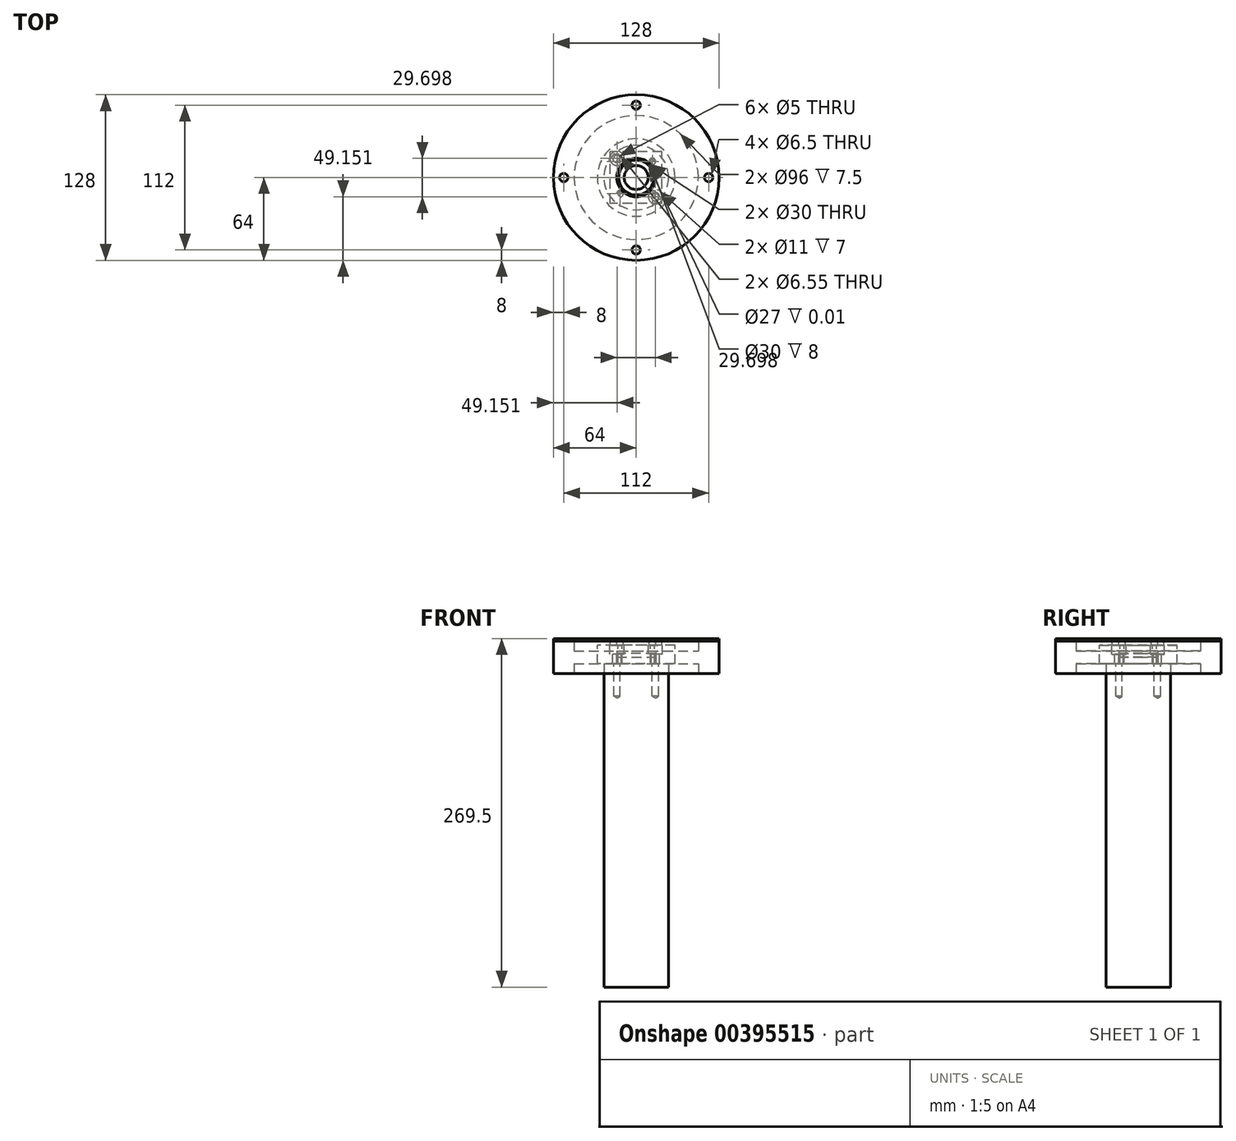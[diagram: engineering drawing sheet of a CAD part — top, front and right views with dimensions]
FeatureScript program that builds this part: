
annotation { "Feature Type Name" : "Feature", "Feature Type Description" : "" }
export const myFeature = defineFeature(function(context is Context, id is Id, definition is map)
    precondition{}
    {
        {
            var Q0;
            Q0=qCreatedBy(makeId("Front.planeOp"),FACE);
            var sketch = newSketch(context, id + "F0", { "sketchPlane" : qUnion([Q0])});
            skLineSegment(sketch, "E0.bottom", {"start": v(-64, 0) * mm, "end": v(-48, 0) * mm});
            skLineSegment(sketch, "E0.top", {"start": v(-64, -25) * mm, "end": v(-48, -25) * mm});
            skLineSegment(sketch, "E0.left", {"start": v(-64, 0) * mm, "end": v(-64, -25) * mm});
            skLineSegment(sketch, "E0.right", {"start": v(-15, -7.5) * mm, "end": v(-15, -17.5) * mm});
            skLineSegment(sketch, "E1", {"start": v(-48, 0) * mm, "end": v(-48, -7.5) * mm});
            skPoint(sketch, "E2.oppositeSnap0", {"position": v(-15, -17.5) * mm});
            skLineSegment(sketch, "E2.bottom", {"start": v(-15, -7.5) * mm, "end": v(-48, -7.5) * mm});
            skLineSegment(sketch, "E2.top", {"start": v(-15, -17.5) * mm, "end": v(-48, -17.5) * mm});
            skLineSegment(sketch, "E3.trimOffspring", {"start": v(-48, -17.5) * mm, "end": v(-48, -25) * mm});
            skSolve(sketch);
        }
        {
            var Q0;
            Q0=qCreatedBy(makeId("Front.planeOp"),FACE);
            var sketch = newSketch(context, id + "F1", { "sketchPlane" : qUnion([Q0])});
            skLineSegment(sketch, "E4.bottom", {"start": v(-25, -267.5) * mm, "end": v(0, -267.5) * mm});
            skLineSegment(sketch, "E4.top", {"start": v(-25, -17.5) * mm, "end": v(-15, -17.5) * mm});
            skLineSegment(sketch, "E4.left", {"start": v(-25, -267.5) * mm, "end": v(-25, -17.5) * mm});
            skLineSegment(sketch, "E4.right", {"start": v(0, -267.5) * mm, "end": v(0, -12.5) * mm});
            skLineSegment(sketch, "E5.top", {"start": v(0, -12.5) * mm, "end": v(-15, -12.5) * mm});
            skLineSegment(sketch, "E5.right", {"start": v(-15, -17.5) * mm, "end": v(-15, -12.5) * mm});
            skSolve(sketch);
        }
        {
            var Q0;
            Q0=makeQuery(id+"F1.imprint","IMPRINT",FACE,{"disambiguationData":[TD([[makeQuery(id+"F1.imprint","IMPRINT",EDGE,{"derivedFrom":sQuery(id+"F1.wireOp",EDGE,"E4.bottom")}),1.0]])]});
            var Q1;
            Q1=sQuery(id+"F1.wireOp",EDGE,"E4.right");
            revolve(context, id + "F2", {"entities" : qUnion([Q0]), "axis" : qUnion([Q1]), "revolveType" : RevolveType.FULL});
        }
        {
            var Q0;
            Q0=makeQuery(id+"F0.imprint","IMPRINT",FACE,{"disambiguationData":[TD([[makeQuery(id+"F0.imprint","IMPRINT",EDGE,{"derivedFrom":sQuery(id+"F0.wireOp",EDGE,"E0.bottom")}),-1.0]])]});
            var Q1;
            Q1=sQuery(id+"F1.wireOp",EDGE,"E4.right");
            revolve(context, id + "F3", {"entities" : qUnion([Q0]), "axis" : qUnion([Q1]), "revolveType" : RevolveType.FULL});
        }
        {
            var Q0;
            Q0=qCreatedBy(makeId("Top.planeOp"),FACE);
            var sketch = newSketch(context, id + "F4", { "sketchPlane" : qUnion([Q0])});
            skCircle(sketch, "E6", {"center": v(0, 0) * mm, "radius": 13.5 * mm});
            skCircle(sketch, "E7", {"center": v(-12.5, 12.5) * mm, "radius": 2.5 * mm});
            skCircle(sketch, "E8", {"center": v(12.5, 12.5) * mm, "radius": 2.5 * mm});
            skCircle(sketch, "E9", {"center": v(12.5, -12.5) * mm, "radius": 2.5 * mm});
            skCircle(sketch, "E10", {"center": v(-12.5, -12.5) * mm, "radius": 2.5 * mm});
            skLineSegment(sketch, "E11", {"start": v(-12.5, 12.5) * mm, "end": v(12.5, 12.5) * mm, "construction": true});
            skLineSegment(sketch, "E12", {"start": v(12.5, 12.5) * mm, "end": v(12.5, -12.5) * mm, "construction": true});
            skLineSegment(sketch, "E13", {"start": v(12.5, -12.5) * mm, "end": v(-12.5, -12.5) * mm, "construction": true});
            skLineSegment(sketch, "E14", {"start": v(-12.5, -12.5) * mm, "end": v(-12.5, 12.5) * mm, "construction": true});
            skCircle(sketch, "E15", {"center": v(0, 0) * mm, "radius": 9.25 * mm});
            skLineSegment(sketch, "E16", {"start": v(12.5, 0) * mm, "end": v(-12.5, 0) * mm, "construction": true});
            skLineSegment(sketch, "E17", {"start": v(0, -12.5) * mm, "end": v(0, 12.5) * mm, "construction": true});
            skLineSegment(sketch, "E18.bottom", {"start": v(20, -20) * mm, "end": v(-20, -20) * mm});
            skLineSegment(sketch, "E18.top", {"start": v(20, 20) * mm, "end": v(-20, 20) * mm});
            skLineSegment(sketch, "E18.left", {"start": v(20, -20) * mm, "end": v(20, 20) * mm});
            skLineSegment(sketch, "E18.right", {"start": v(-20, -20) * mm, "end": v(-20, 20) * mm});
            skSolve(sketch);
        }
        {
            var Q0;
            Q0=makeQuery(id+"F4.imprint","IMPRINT",FACE,{"disambiguationData":[TD([[makeQuery(id+"F4.imprint","IMPRINT",EDGE,{"derivedFrom":sQuery(id+"F4.wireOp",EDGE,"E6")}),-1.0]])]});
            var Q1;
            Q1=makeQuery(id+"F4.imprint","IMPRINT",FACE,{"disambiguationData":[TD([[makeQuery(id+"F4.imprint","IMPRINT",EDGE,{"derivedFrom":sQuery(id+"F4.wireOp",EDGE,"E6")}),1.0]])]});
            var Q2;
            Q2=makeQuery(id+"F4.imprint","IMPRINT",FACE,{"disambiguationData":[TD([[makeQuery(id+"F4.imprint","IMPRINT",EDGE,{"derivedFrom":sQuery(id+"F4.wireOp",EDGE,"E15")}),1.0]])]});
            extrude(context, id + "F5", {"entities" : qUnion([Q0, Q1, Q2]), "depth" : -3 * mm});
        }
        {
            var Q0;
            Q0=makeQuery(id+"F4.imprint","IMPRINT",FACE,{"disambiguationData":[TD([[makeQuery(id+"F4.imprint","IMPRINT",EDGE,{"derivedFrom":sQuery(id+"F4.wireOp",EDGE,"E6")}),1.0]])]});
            extrude(context, id + "F6", {"entities" : qUnion([Q0]), "operationType" : NewBodyOperationType.REMOVE, "depth" : -0.01 * mm});
        }
        {
            var Q0;
            Q0=qCreatedBy(makeId("Top.planeOp"),FACE);
            var sketch = newSketch(context, id + "F7", { "sketchPlane" : qUnion([Q0])});
            skCircle(sketch, "E19", {"center": v(0, 0) * mm, "radius": 64 * mm});
            skCircle(sketch, "E20", {"center": v(0, 0) * mm, "radius": 56 * mm, "construction": true});
            skLineSegment(sketch, "E21", {"start": v(0, 0) * mm, "end": v(0, 56) * mm, "construction": true});
            skLineSegment(sketch, "E22", {"start": v(0, 0) * mm, "end": v(-56, 0) * mm, "construction": true});
            skLineSegment(sketch, "E23", {"start": v(0, 0) * mm, "end": v(56, 0) * mm, "construction": true});
            skLineSegment(sketch, "E24", {"start": v(0, 0) * mm, "end": v(0, -56) * mm, "construction": true});
            skCircle(sketch, "E25", {"center": v(-56, 0) * mm, "radius": 3.25 * mm});
            skCircle(sketch, "E26", {"center": v(0, 56) * mm, "radius": 3.25 * mm});
            skCircle(sketch, "E27", {"center": v(56, 0) * mm, "radius": 3.25 * mm});
            skCircle(sketch, "E28", {"center": v(0, -56) * mm, "radius": 3.25 * mm});
            skCircle(sketch, "E29", {"center": v(0, 0) * mm, "radius": 15 * mm});
            skSolve(sketch);
        }
        {
            var Q0;
            Q0=makeQuery(id+"F7.imprint","IMPRINT",FACE,{"disambiguationData":[TD([[makeQuery(id+"F7.imprint","IMPRINT",EDGE,{"derivedFrom":sQuery(id+"F7.wireOp",EDGE,"E19")}),1.0]])]});
            extrude(context, id + "F8", {"entities" : qUnion([Q0]), "depth" : 2 * mm});
        }
        {
            var Q0;
            Q0=qCreatedBy(makeId("Top.planeOp"),FACE);
            var sketch = newSketch(context, id + "F9", { "sketchPlane" : qUnion([Q0])});
            skCircle(sketch, "E30", {"center": v(0, 0) * mm, "radius": 30 * mm});
            skCircle(sketch, "E31", {"center": v(12.5, 12.5) * mm, "radius": 2.5 * mm, "construction": true});
            skCircle(sketch, "E32", {"center": v(-12.5, -12.5) * mm, "radius": 2.5 * mm, "construction": true});
            skCircle(sketch, "E33", {"center": v(0, 0) * mm, "radius": 17.68 * mm, "construction": true});
            skLineSegment(sketch, "E34", {"start": v(0, 0) * mm, "end": v(12.5, 12.5) * mm, "construction": true});
            skLineSegment(sketch, "E35", {"start": v(-12.5, -12.5) * mm, "end": v(0, 0) * mm, "construction": true});
            skCircle(sketch, "E36", {"center": v(0, 0) * mm, "radius": 21 * mm, "construction": true});
            skLineSegment(sketch, "E37", {"start": v(-14.85, 14.85) * mm, "end": v(0, 0) * mm, "construction": true});
            skLineSegment(sketch, "E38", {"start": v(14.85, -14.85) * mm, "end": v(0, 0) * mm, "construction": true});
            skCircle(sketch, "E39", {"center": v(14.85, -14.85) * mm, "radius": 3 * mm, "construction": true});
            skCircle(sketch, "E40", {"center": v(-14.85, 14.85) * mm, "radius": 3 * mm, "construction": true});
            skSolve(sketch);
        }
        {
            var Q0;
            Q0=qCreatedBy(makeId("Front.planeOp"),FACE);
            var sketch = newSketch(context, id + "F10", { "sketchPlane" : qUnion([Q0])});
            skLineSegment(sketch, "E41.bottom", {"start": v(-30, -3) * mm, "end": v(0, -3) * mm});
            skLineSegment(sketch, "E41.top", {"start": v(-30, -17.5) * mm, "end": v(-15, -17.5) * mm});
            skLineSegment(sketch, "E41.left", {"start": v(-30, -3) * mm, "end": v(-30, -17.5) * mm});
            skLineSegment(sketch, "E41.right", {"start": v(0, -3) * mm, "end": v(0, -9.5) * mm});
            skLineSegment(sketch, "E42", {"start": v(-15, -17.5) * mm, "end": v(-15, -9.5) * mm});
            skLineSegment(sketch, "E43", {"start": v(-15, -9.5) * mm, "end": v(0, -9.5) * mm});
            skPoint(sketch, "E44.orphan", {"position": v(-15, -21.02) * mm});
            skSolve(sketch);
        }
        {
            var Q0;
            Q0=makeQuery(id+"F10.imprint","IMPRINT",FACE,{"disambiguationData":[TD([[makeQuery(id+"F10.imprint","IMPRINT",EDGE,{"derivedFrom":sQuery(id+"F10.wireOp",EDGE,"E41.bottom")}),-1.0]])]});
            var Q1;
            Q1=sQuery(id+"F10.wireOp",EDGE,"E41.right");
            revolve(context, id + "F11", {"entities" : qUnion([Q0]), "axis" : qUnion([Q1]), "revolveType" : RevolveType.FULL});
        }
        {
            var Q0;
            Q0=sQuery(id+"F9.wireOp",VERTEX,"E32.center");
            var Q1;
            Q1=sQuery(id+"F9.wireOp",VERTEX,"E31.center");
            var Q2;
            Q2=makeQuery(id+"F11.opRevolve","SWEPT_BODY",BODY,{"disambiguationData":[OSD([sQuery(id+"F10.wireOp",EDGE,"E41.bottom"),sQuery(id+"F10.wireOp",EDGE,"E41.top"),sQuery(id+"F10.wireOp",EDGE,"E41.left"),sQuery(id+"F10.wireOp",EDGE,"E41.right"),sQuery(id+"F10.wireOp",EDGE,"E42"),sQuery(id+"F10.wireOp",EDGE,"E43")])]});
            hole(context, id + "F12", {"style" : HoleStyle.SIMPLE, "endStyle" : HoleEndStyle.THROUGH, "holeDiameter" : 3.3 * mm, "isTappedThrough" : true, "tappedDepth" : 12 * mm, "tapClearance" : 3, "locations" : qUnion([Q0, Q1]), "scope" : qUnion([Q2])});
        }
        {
            var Q0;
            Q0=sQuery(id+"F9.wireOp",VERTEX,"E37.start");
            var Q1;
            Q1=sQuery(id+"F9.wireOp",VERTEX,"E38.start");
            var Q2;
            Q2=makeQuery(id+"F11.opRevolve","SWEPT_BODY",BODY,{"disambiguationData":[OSD([sQuery(id+"F10.wireOp",EDGE,"E41.bottom"),sQuery(id+"F10.wireOp",EDGE,"E41.top"),sQuery(id+"F10.wireOp",EDGE,"E41.left"),sQuery(id+"F10.wireOp",EDGE,"E41.right"),sQuery(id+"F10.wireOp",EDGE,"E42"),sQuery(id+"F10.wireOp",EDGE,"E43")])]});
            hole(context, id + "F13", {"style" : HoleStyle.C_BORE, "endStyle" : HoleEndStyle.THROUGH, "holeDiameter" : 6.55 * mm, "cBoreDiameter" : 11 * mm, "cBoreDepth" : 7 * mm, "isTappedThrough" : true, "tappedDepth" : 12 * mm, "tapClearance" : 3, "locations" : qUnion([Q0, Q1]), "scope" : qUnion([Q2])});
        }
        {
            var Q0;
            Q0=sQuery(id+"F9.wireOp",VERTEX,"E38.start");
            var Q1;
            Q1=sQuery(id+"F9.wireOp",VERTEX,"E37.start");
            var Q2;
            Q2=makeQuery(id+"F2.opRevolve","SWEPT_BODY",BODY,{"disambiguationData":[OSD([sQuery(id+"F1.wireOp",EDGE,"E4.bottom"),sQuery(id+"F1.wireOp",EDGE,"E4.top"),sQuery(id+"F1.wireOp",EDGE,"E4.left"),sQuery(id+"F1.wireOp",EDGE,"E4.right"),sQuery(id+"F1.wireOp",EDGE,"E5.top"),sQuery(id+"F1.wireOp",EDGE,"E5.right")])]});
            hole(context, id + "F14", {"style" : HoleStyle.SIMPLE, "endStyle" : HoleEndStyle.BLIND, "holeDiameter" : 5 * mm, "holeDepth" : 25 * mm, "isTappedThrough" : true, "tappedDepth" : 12 * mm, "tapClearance" : 3, "locations" : qUnion([Q0, Q1]), "scope" : qUnion([Q2])});
        }
    });
